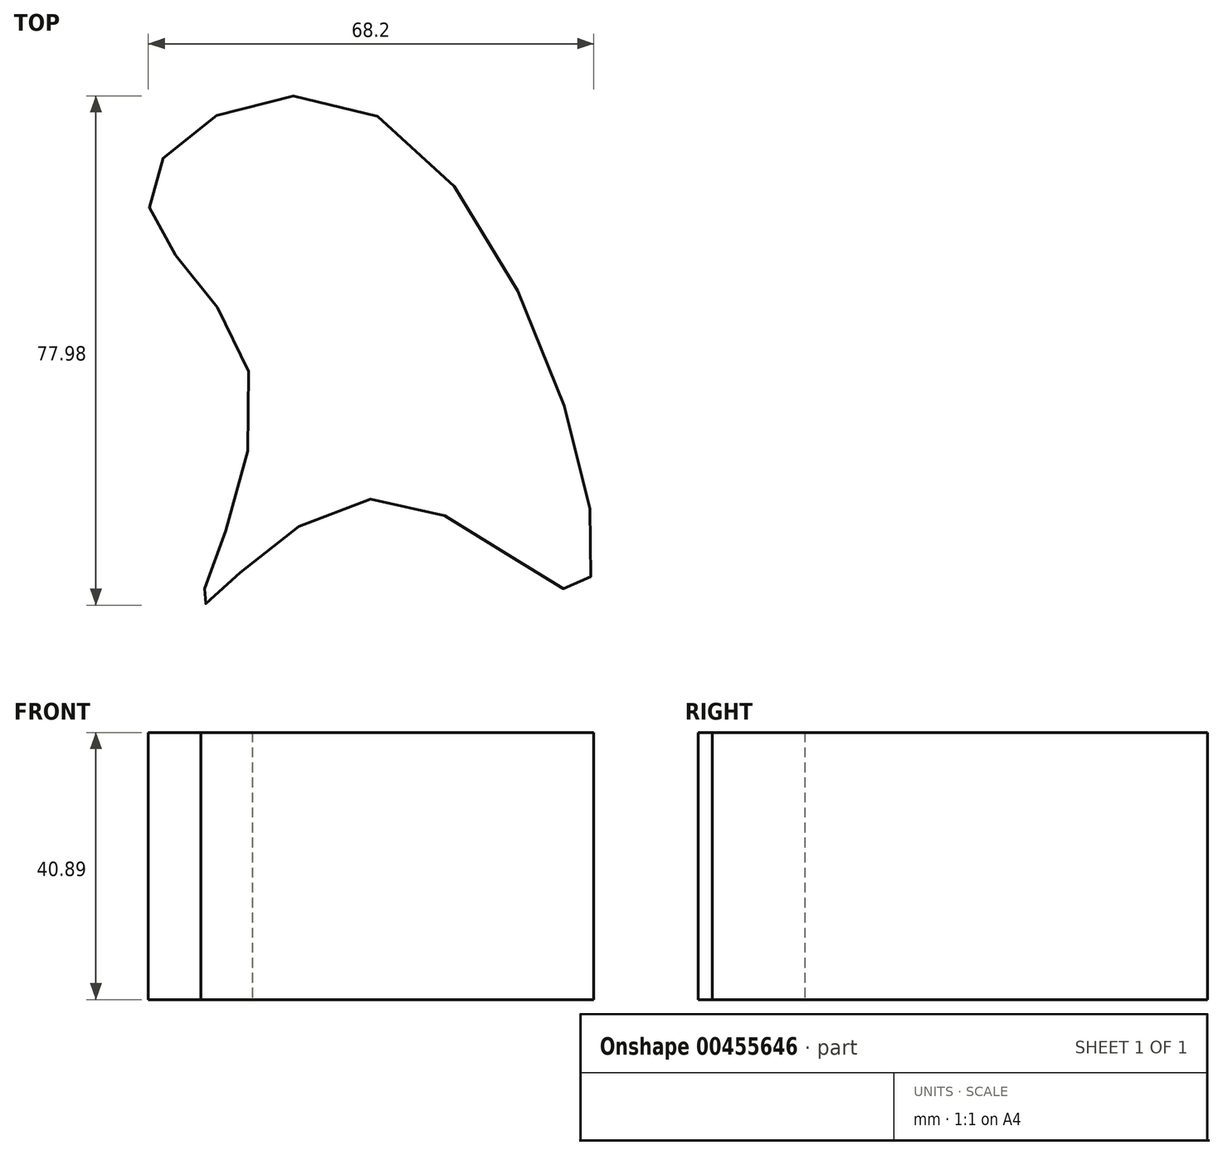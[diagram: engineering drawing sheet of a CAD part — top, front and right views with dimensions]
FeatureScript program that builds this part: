
annotation { "Feature Type Name" : "Feature", "Feature Type Description" : "" }
export const myFeature = defineFeature(function(context is Context, id is Id, definition is map)
    precondition{}
    {
        {
            var Q0;
            Q0=qCreatedBy(makeId("Top.planeOp"),FACE);
            var sketch = newSketch(context, id + "F0", { "sketchPlane" : qUnion([Q0])});
            skFitSpline(sketch, "E0", {"points": [v(0, 40.57) * mm, v(-35.01, 29.09) * mm, v(-19.45, 0) * mm, v(-26.86, -34.27) * mm, v(0, -17.97) * mm, v(31.68, -31.68) * mm, v(0, 40.57) * mm]});
            skSolve(sketch);
        }
        {
            var Q0;
            Q0=makeQuery(id+"F0.imprint","IMPRINT",FACE,{"disambiguationData":[TD([[makeQuery(id+"F0.imprint","IMPRINT",EDGE,{"derivedFrom":sQuery(id+"F0.wireOp",EDGE,"E0")}),1.0]])]});
            extrude(context, id + "F1", {"entities" : qUnion([Q0]), "depth" : 40.9 * mm});
        }
    });
